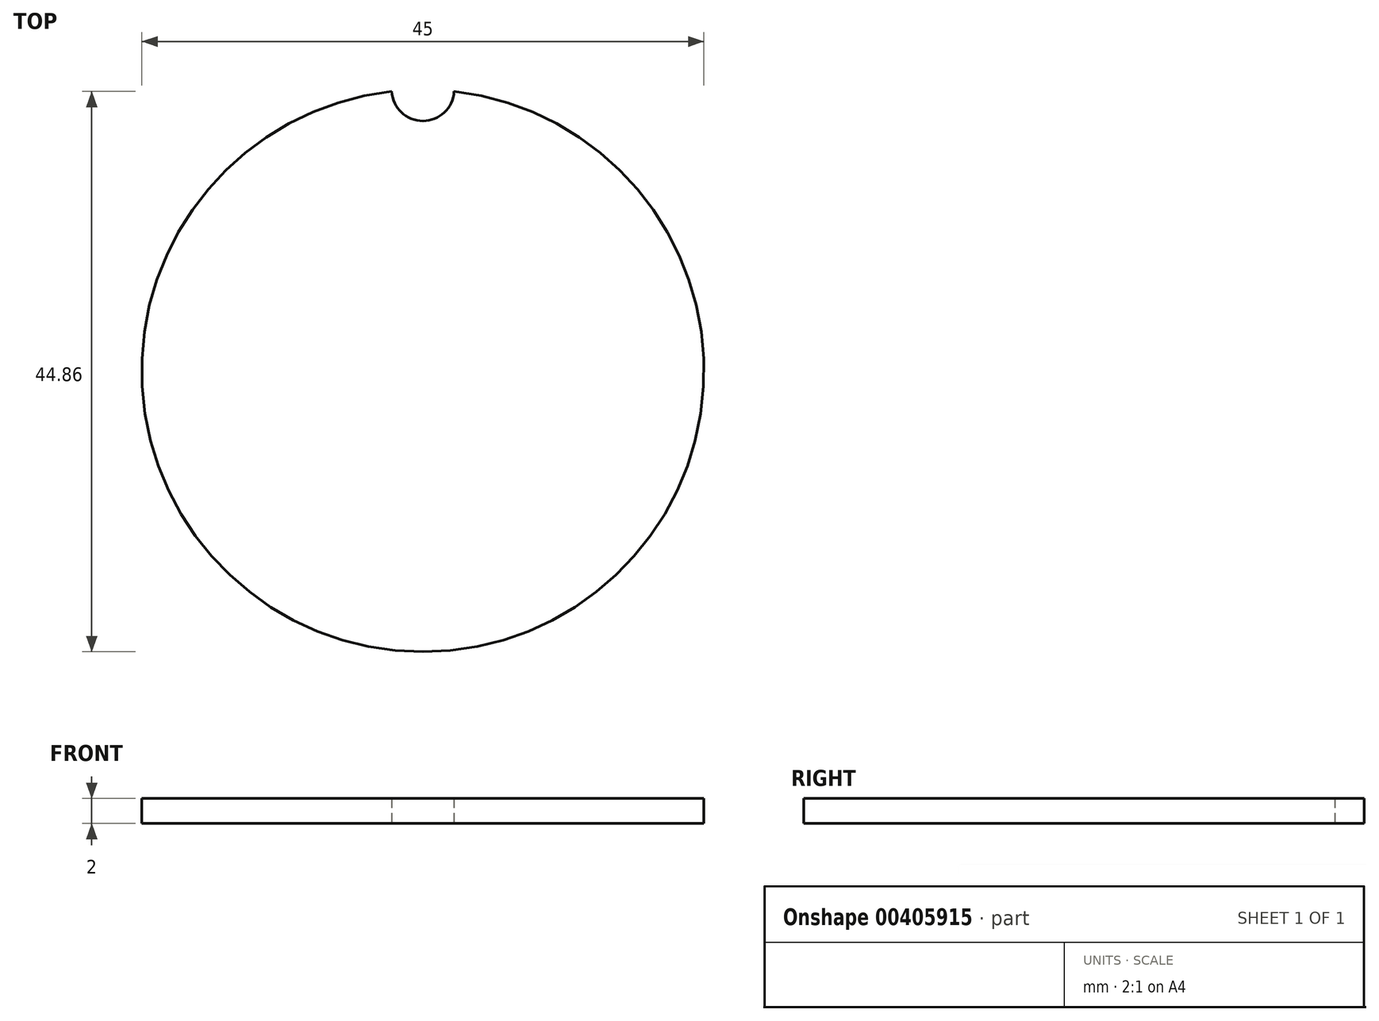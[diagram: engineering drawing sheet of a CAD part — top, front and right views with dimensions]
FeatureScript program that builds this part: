
annotation { "Feature Type Name" : "Feature", "Feature Type Description" : "" }
export const myFeature = defineFeature(function(context is Context, id is Id, definition is map)
    precondition{}
    {
        {
            var Q0;
            Q0=qCreatedBy(makeId("Top.planeOp"),FACE);
            var sketch = newSketch(context, id + "F0", { "sketchPlane" : qUnion([Q0])});
            skCircle(sketch, "E0", {"center": v(0, 0) * mm, "radius": 25 * mm});
            skArc(sketch, "E1", {"start": v(-2.5, 22.36) * mm, "mid": v(0, -22.5) * mm, "end": v(2.5, 22.36) * mm});
            skCircle(sketch, "E2", {"center": v(0, 22.5) * mm, "radius": 2.5 * mm});
            skCircle(sketch, "E3", {"center": v(0, 22.5) * mm, "radius": 1.88 * mm});
            skCircle(sketch, "E4", {"center": v(0, 22.5) * mm, "radius": 1.25 * mm});
            skSolve(sketch);
        }
        {
            var Q0;
            {var subQ0=sQuery(id+"F0.wireOp",EDGE,"E1");Q0=makeQuery(id+"F0.imprint","IMPRINT",FACE,{"disambiguationData":[TD([[makeQuery(id+"F0.imprint","IMPRINT",EDGE,{"derivedFrom":subQ0}),1.0]])]});}
            extrude(context, id + "F1", {"entities" : qUnion([Q0]), "depth" : 2 * mm});
        }
    });
